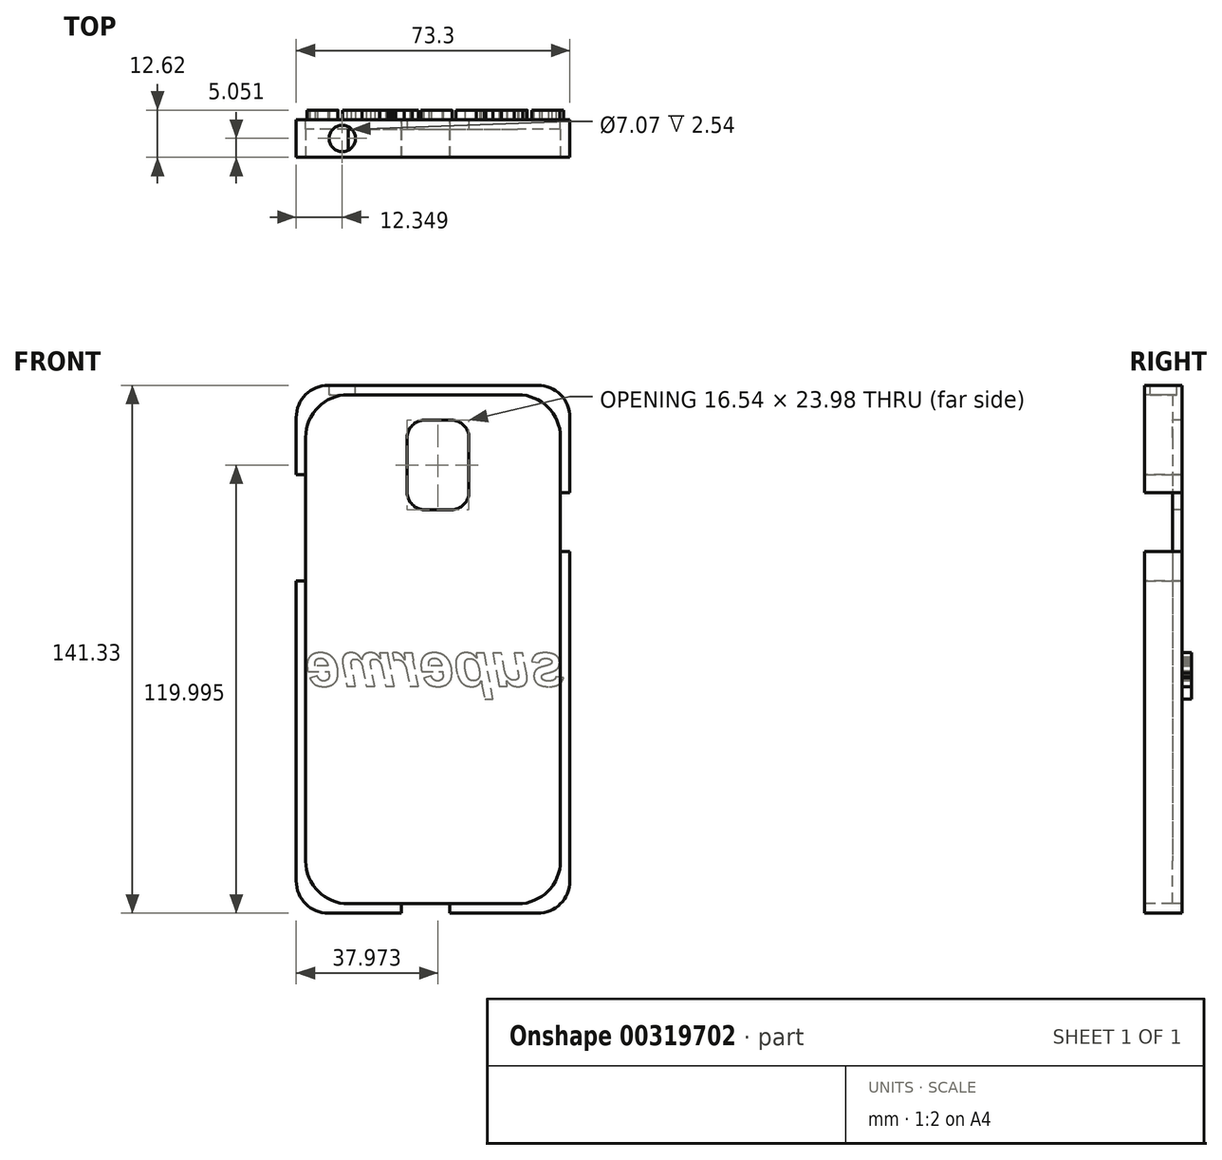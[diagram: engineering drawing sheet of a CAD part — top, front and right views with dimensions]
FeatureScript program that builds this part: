
annotation { "Feature Type Name" : "Feature", "Feature Type Description" : "" }
export const myFeature = defineFeature(function(context is Context, id is Id, definition is map)
    precondition{}
    {
        {
            var Q0;
            Q0=qCreatedBy(makeId("Front.planeOp"),FACE);
            var sketch = newSketch(context, id + "F0", { "sketchPlane" : qUnion([Q0])});
            skLineSegment(sketch, "E0.bottom", {"start": v(-58.25, 68.55) * mm, "end": v(15.05, 68.55) * mm});
            skLineSegment(sketch, "E0.top", {"start": v(-58.25, -72.78) * mm, "end": v(15.05, -72.78) * mm});
            skLineSegment(sketch, "E0.left", {"start": v(-58.25, 68.55) * mm, "end": v(-58.25, -72.78) * mm});
            skLineSegment(sketch, "E0.right", {"start": v(15.05, 68.55) * mm, "end": v(15.05, -72.78) * mm});
            skLineSegment(sketch, "E1.bottom", {"start": v(-23.48, 54.28) * mm, "end": v(-18.56, 54.28) * mm});
            skLineSegment(sketch, "E1.top", {"start": v(-23.48, 32.28) * mm, "end": v(-18.56, 32.28) * mm});
            skLineSegment(sketch, "E1.left", {"start": v(-26.02, 51.74) * mm, "end": v(-26.02, 34.82) * mm});
            skLineSegment(sketch, "E1.right", {"start": v(-16.02, 51.74) * mm, "end": v(-16.02, 34.82) * mm});
            skPoint(sketch, "E2.visualSharp", {"position": v(-26.02, 54.28) * mm});
            skArc(sketch, "E2.filletArc", {"start": v(-23.48, 54.28) * mm, "mid": v(-25.28, 53.54) * mm, "end": v(-26.02, 51.74) * mm});
            skPoint(sketch, "E3.visualSharp", {"position": v(-26.02, 32.28) * mm});
            skArc(sketch, "E3.filletArc", {"start": v(-26.02, 34.82) * mm, "mid": v(-25.28, 33.03) * mm, "end": v(-23.48, 32.28) * mm});
            skLineSegment(sketch, "E4.bottom", {"start": v(-52.76, -64.42) * mm, "end": v(-45.27, -64.42) * mm});
            skLineSegment(sketch, "E4.top", {"start": v(-52.76, -69.42) * mm, "end": v(-45.27, -69.42) * mm});
            skLineSegment(sketch, "E4.left", {"start": v(-53.01, -64.68) * mm, "end": v(-53.01, -69.17) * mm});
            skLineSegment(sketch, "E4.right", {"start": v(-45.01, -64.68) * mm, "end": v(-45.01, -69.17) * mm});
            skPoint(sketch, "E5.visualSharp", {"position": v(-16.02, 54.28) * mm});
            skArc(sketch, "E5.filletArc", {"start": v(-16.02, 51.74) * mm, "mid": v(-16.76, 53.54) * mm, "end": v(-18.56, 54.28) * mm});
            skPoint(sketch, "E6.visualSharp", {"position": v(-16.02, 32.28) * mm});
            skArc(sketch, "E6.filletArc", {"start": v(-18.56, 32.28) * mm, "mid": v(-16.76, 33.03) * mm, "end": v(-16.02, 34.82) * mm});
            skPoint(sketch, "E7.visualSharp", {"position": v(-53.01, -64.42) * mm});
            skArc(sketch, "E7.filletArc", {"start": v(-52.76, -64.42) * mm, "mid": v(-52.94, -64.5) * mm, "end": v(-53.01, -64.68) * mm});
            skPoint(sketch, "E8.visualSharp", {"position": v(-53.01, -69.42) * mm});
            skArc(sketch, "E8.filletArc", {"start": v(-53.01, -69.17) * mm, "mid": v(-52.94, -69.35) * mm, "end": v(-52.76, -69.42) * mm});
            skPoint(sketch, "E9.visualSharp", {"position": v(-45.01, -64.42) * mm});
            skArc(sketch, "E9.filletArc", {"start": v(-45.01, -64.68) * mm, "mid": v(-45.09, -64.5) * mm, "end": v(-45.27, -64.42) * mm});
            skPoint(sketch, "E10.visualSharp", {"position": v(-45.01, -69.42) * mm});
            skArc(sketch, "E10.filletArc", {"start": v(-45.27, -69.42) * mm, "mid": v(-45.09, -69.35) * mm, "end": v(-45.01, -69.17) * mm});
            skLineSegment(sketch, "E11.0", {"start": v(-55.71, 66) * mm, "end": v(12.51, 66) * mm});
            skLineSegment(sketch, "E11.1", {"start": v(-55.71, 66) * mm, "end": v(-55.71, -70.24) * mm});
            skLineSegment(sketch, "E11.2", {"start": v(-55.71, -70.24) * mm, "end": v(12.51, -70.24) * mm});
            skLineSegment(sketch, "E11.3", {"start": v(12.51, 66) * mm, "end": v(12.51, -70.24) * mm});
            skSolve(sketch);
        }
        {
            var Q0;
            Q0=makeQuery(id+"F0.imprint","IMPRINT",FACE,{"disambiguationData":[TD([[makeQuery(id+"F0.imprint","IMPRINT",EDGE,{"derivedFrom":sQuery(id+"F0.wireOp",EDGE,"E0.bottom")}),-1.0]])]});
            extrude(context, id + "F1", {"entities" : qUnion([Q0]), "oppositeDirection" : true, "depth" : 10.08 * mm});
        }
        {
            var Q0;
            Q0=makeQuery(id+"F1.opExtrude","CAP_FACE",FACE,{"disambiguationData":[OSD([sQuery(id+"F0.wireOp",EDGE,"E0.bottom"),sQuery(id+"F0.wireOp",EDGE,"E0.top"),sQuery(id+"F0.wireOp",EDGE,"E0.left"),sQuery(id+"F0.wireOp",EDGE,"E0.right"),sQuery(id+"F0.wireOp",EDGE,"E11.0"),sQuery(id+"F0.wireOp",EDGE,"E11.1"),sQuery(id+"F0.wireOp",EDGE,"E11.2"),sQuery(id+"F0.wireOp",EDGE,"E11.3")])],"isStart":false});
            var sketch = newSketch(context, id + "F2", { "sketchPlane" : qUnion([Q0])});
            skSolve(sketch);
        }
        {
            var Q0;
            Q0=makeQuery(id+"F2.imprint","IMPRINT",FACE,{"disambiguationData":[TD([[makeQuery(id+"F2.imprint","IMPRINT",EDGE,{"derivedFrom":makeQuery(id+"F1.opExtrude","CAP_EDGE",EDGE,{"disambiguationData":[OSD([sQuery(id+"F0.wireOp",EDGE,"E11.0")])],"isStart":false})}),1.0]])]});
            var Q1;
            Q1=makeQuery(id+"F2.imprint","IMPRINT",FACE,{"disambiguationData":[TD([[makeQuery(id+"F2.imprint","IMPRINT",EDGE,{"derivedFrom":makeQuery(id+"F1.opExtrude","CAP_EDGE",EDGE,{"disambiguationData":[OSD([sQuery(id+"F0.wireOp",EDGE,"E0.bottom")])],"isStart":false})}),1.0]])]});
            extrude(context, id + "F3", {"entities" : qUnion([Q0, Q1]), "operationType" : NewBodyOperationType.ADD, "oppositeDirection" : true, "depth" : 2.54 * mm});
        }
        {
            var Q0;
            {var subQ0=sQuery(id+"F0.wireOp",EDGE,"E0.right");var subQ1=sQuery(id+"F0.wireOp",EDGE,"E0.left");var subQ2=sQuery(id+"F0.wireOp",EDGE,"E0.top");var subQ3=sQuery(id+"F0.wireOp",EDGE,"E0.bottom");Q0=makeQuery(id+"F3.boolean.opBoolean","MERGE",FACE,{"derivedFrom":[makeQuery(id+"F1.opExtrude","CAP_FACE",FACE,{"disambiguationData":[OSD([subQ3,subQ2,subQ1,subQ0,sQuery(id+"F0.wireOp",EDGE,"E11.0"),sQuery(id+"F0.wireOp",EDGE,"E11.1"),sQuery(id+"F0.wireOp",EDGE,"E11.2"),sQuery(id+"F0.wireOp",EDGE,"E11.3")])],"isStart":false}),makeQuery(id+"F3.opExtrude","CAP_FACE",FACE,{"disambiguationData":[OSD([subQ3,subQ2,subQ1,subQ0])],"isStart":true})]});}
            var sketch = newSketch(context, id + "F4", { "sketchPlane" : qUnion([Q0])});
            skSolve(sketch);
        }
        {
            var Q0;
            Q0=makeQuery(id+"F1.opExtrude","SWEPT_FACE",FACE,{"disambiguationData":[OSD([sQuery(id+"F0.wireOp",EDGE,"E0.left")])]});
            var sketch = newSketch(context, id + "F5", { "sketchPlane" : qUnion([Q0])});
            skLineSegment(sketch, "E12.bottom", {"start": v(-10.08, 44.57) * mm, "end": v(0, 44.57) * mm});
            skLineSegment(sketch, "E12.top", {"start": v(-10.08, 16.2) * mm, "end": v(0, 16.2) * mm});
            skLineSegment(sketch, "E12.left", {"start": v(0, 44.57) * mm, "end": v(0, 16.2) * mm});
            skLineSegment(sketch, "E12.right", {"start": v(-10.08, 44.57) * mm, "end": v(-10.08, 16.2) * mm});
            skSolve(sketch);
        }
        {
            var Q0;
            Q0=makeQuery(id+"F1.opExtrude","SWEPT_FACE",FACE,{"disambiguationData":[OSD([sQuery(id+"F0.wireOp",EDGE,"E0.right")])]});
            var sketch = newSketch(context, id + "F6", { "sketchPlane" : qUnion([Q0])});
            skLineSegment(sketch, "E13.bottom", {"start": v(0, 39.75) * mm, "end": v(10.08, 39.75) * mm});
            skLineSegment(sketch, "E13.top", {"start": v(0, 24.1) * mm, "end": v(10.08, 24.1) * mm});
            skLineSegment(sketch, "E13.left", {"start": v(10.08, 39.75) * mm, "end": v(10.08, 24.1) * mm});
            skLineSegment(sketch, "E13.right", {"start": v(0, 39.75) * mm, "end": v(0, 24.1) * mm});
            skSolve(sketch);
        }
        {
            var Q0;
            Q0=makeQuery(id+"F1.opExtrude","SWEPT_FACE",FACE,{"disambiguationData":[OSD([sQuery(id+"F0.wireOp",EDGE,"E0.top")])]});
            var sketch = newSketch(context, id + "F7", { "sketchPlane" : qUnion([Q0])});
            skLineSegment(sketch, "E14.bottom", {"start": v(-30.14, -10.08) * mm, "end": v(-17.14, -10.08) * mm});
            skLineSegment(sketch, "E14.top", {"start": v(-30.14, 0) * mm, "end": v(-17.14, 0) * mm});
            skLineSegment(sketch, "E14.left", {"start": v(-30.14, 0) * mm, "end": v(-30.14, -10.08) * mm});
            skLineSegment(sketch, "E14.right", {"start": v(-17.14, 0) * mm, "end": v(-17.14, -10.08) * mm});
            skSolve(sketch);
        }
        {
            var Q0;
            Q0=makeQuery(id+"F7.imprint","IMPRINT",FACE,{"disambiguationData":[TD([[makeQuery(id+"F7.imprint","IMPRINT",EDGE,{"derivedFrom":sQuery(id+"F7.wireOp",EDGE,"E14.bottom")}),1.0]])]});
            var Q1;
            Q1=makeQuery(id+"F1.opExtrude","SWEPT_FACE",FACE,{"disambiguationData":[OSD([sQuery(id+"F0.wireOp",EDGE,"E11.2")])]});
            extrude(context, id + "F8", {"entities" : qUnion([Q0]), "operationType" : NewBodyOperationType.REMOVE, "endBound" : BoundingType.UP_TO_SURFACE, "oppositeDirection" : true, "endBoundEntityFace" : qUnion([Q1]), "depth" : 25.4 * mm});
        }
        {
            var Q0;
            Q0=makeQuery(id+"F5.imprint","IMPRINT",FACE,{"disambiguationData":[TD([[makeQuery(id+"F5.imprint","IMPRINT",EDGE,{"derivedFrom":sQuery(id+"F5.wireOp",EDGE,"E12.bottom")}),-1.0]])]});
            var Q1;
            Q1=makeQuery(id+"F1.opExtrude","SWEPT_FACE",FACE,{"disambiguationData":[OSD([sQuery(id+"F0.wireOp",EDGE,"E11.1")])]});
            extrude(context, id + "F9", {"entities" : qUnion([Q0]), "operationType" : NewBodyOperationType.REMOVE, "endBound" : BoundingType.UP_TO_SURFACE, "oppositeDirection" : true, "endBoundEntityFace" : qUnion([Q1]), "depth" : 25.4 * mm});
        }
        {
            var Q0;
            Q0=makeQuery(id+"F6.imprint","IMPRINT",FACE,{"disambiguationData":[TD([[makeQuery(id+"F6.imprint","IMPRINT",EDGE,{"derivedFrom":sQuery(id+"F6.wireOp",EDGE,"E13.bottom")}),-1.0]])]});
            var Q1;
            Q1=makeQuery(id+"F1.opExtrude","SWEPT_FACE",FACE,{"disambiguationData":[OSD([sQuery(id+"F0.wireOp",EDGE,"E11.3")])]});
            extrude(context, id + "F10", {"entities" : qUnion([Q0]), "operationType" : NewBodyOperationType.REMOVE, "endBound" : BoundingType.UP_TO_SURFACE, "oppositeDirection" : true, "endBoundEntityFace" : qUnion([Q1]), "depth" : 25.4 * mm});
        }
        {
            var Q0;
            Q0=makeQuery(id+"F1.opExtrude","SWEPT_FACE",FACE,{"disambiguationData":[OSD([sQuery(id+"F0.wireOp",EDGE,"E0.bottom")])]});
            var sketch = newSketch(context, id + "F11", { "sketchPlane" : qUnion([Q0])});
            skCircle(sketch, "E15", {"center": v(-45.9, 5.05) * mm, "radius": 3.53 * mm});
            skSolve(sketch);
        }
        {
            var Q0;
            Q0=makeQuery(id+"F11.imprint","IMPRINT",FACE,{"disambiguationData":[TD([[makeQuery(id+"F11.imprint","IMPRINT",EDGE,{"derivedFrom":sQuery(id+"F11.wireOp",EDGE,"E15")}),1.0]])]});
            var Q1;
            Q1=makeQuery(id+"F1.opExtrude","SWEPT_FACE",FACE,{"disambiguationData":[OSD([sQuery(id+"F0.wireOp",EDGE,"E11.0")])]});
            extrude(context, id + "F12", {"entities" : qUnion([Q0]), "operationType" : NewBodyOperationType.REMOVE, "endBound" : BoundingType.UP_TO_SURFACE, "oppositeDirection" : true, "endBoundEntityFace" : qUnion([Q1]), "depth" : 25.4 * mm});
        }
        {
            var Q0;
            Q0=makeQuery(id+"F1.opExtrude","SWEPT_EDGE",EDGE,{"disambiguationData":[OSD([sQuery(id+"F0.wireOp",EDGE,"E0.bottom"),sQuery(id+"F0.wireOp",EDGE,"E0.right")])]});
            var Q1;
            Q1=makeQuery(id+"F1.opExtrude","SWEPT_EDGE",EDGE,{"disambiguationData":[OSD([sQuery(id+"F0.wireOp",EDGE,"E0.bottom"),sQuery(id+"F0.wireOp",EDGE,"E0.left")])]});
            var Q2;
            Q2=makeQuery(id+"F1.opExtrude","SWEPT_EDGE",EDGE,{"disambiguationData":[OSD([sQuery(id+"F0.wireOp",EDGE,"E0.top"),sQuery(id+"F0.wireOp",EDGE,"E0.right")])]});
            var Q3;
            Q3=makeQuery(id+"F1.opExtrude","SWEPT_EDGE",EDGE,{"disambiguationData":[OSD([sQuery(id+"F0.wireOp",EDGE,"E0.top"),sQuery(id+"F0.wireOp",EDGE,"E0.left")])]});
            fillet(context, id + "F13", {"entities" : qUnion([Q0, Q1, Q2, Q3]), "radius" : 8.64 * mm, "tangentPropagation" : true, "allowEdgeOverflow" : false});
        }
        {
            var Q0;
            Q0=makeQuery(id+"F1.opExtrude","SWEPT_EDGE",EDGE,{"disambiguationData":[OSD([sQuery(id+"F0.wireOp",EDGE,"E11.0"),sQuery(id+"F0.wireOp",EDGE,"E11.1")])]});
            var Q1;
            Q1=makeQuery(id+"F1.opExtrude","SWEPT_EDGE",EDGE,{"disambiguationData":[OSD([sQuery(id+"F0.wireOp",EDGE,"E11.2"),sQuery(id+"F0.wireOp",EDGE,"E11.3")])]});
            var Q2;
            Q2=makeQuery(id+"F1.opExtrude","SWEPT_EDGE",EDGE,{"disambiguationData":[OSD([sQuery(id+"F0.wireOp",EDGE,"E11.0"),sQuery(id+"F0.wireOp",EDGE,"E11.3")])]});
            var Q3;
            Q3=makeQuery(id+"F1.opExtrude","SWEPT_EDGE",EDGE,{"disambiguationData":[OSD([sQuery(id+"F0.wireOp",EDGE,"E11.1"),sQuery(id+"F0.wireOp",EDGE,"E11.2")])]});
            fillet(context, id + "F14", {"entities" : qUnion([Q0, Q1, Q2, Q3]), "radius" : 11.43 * mm, "tangentPropagation" : true, "allowEdgeOverflow" : false});
        }
        {
            var Q0;
            Q0=makeQuery(id+"F3.opExtrude","CAP_FACE",FACE,{"disambiguationData":[OSD([sQuery(id+"F0.wireOp",EDGE,"E0.bottom"),sQuery(id+"F0.wireOp",EDGE,"E0.top"),sQuery(id+"F0.wireOp",EDGE,"E0.left"),sQuery(id+"F0.wireOp",EDGE,"E0.right")])],"isStart":false});
            var sketch = newSketch(context, id + "F15", { "sketchPlane" : qUnion([Q0])});
            skLineSegment(sketch, "E16.bottom", {"start": v(-28.55, 59.2) * mm, "end": v(-12, 59.2) * mm});
            skLineSegment(sketch, "E16.top", {"start": v(-28.55, 35.23) * mm, "end": v(-12, 35.23) * mm});
            skLineSegment(sketch, "E16.left", {"start": v(-28.55, 59.2) * mm, "end": v(-28.55, 35.23) * mm});
            skLineSegment(sketch, "E16.right", {"start": v(-12, 59.2) * mm, "end": v(-12, 35.23) * mm});
            skSolve(sketch);
        }
        {
            var Q0;
            Q0=makeQuery(id+"F15.imprint","IMPRINT",FACE,{"disambiguationData":[TD([[makeQuery(id+"F15.imprint","IMPRINT",EDGE,{"derivedFrom":sQuery(id+"F15.wireOp",EDGE,"E16.bottom")}),-1.0]])]});
            var Q1;
            {var subQ0=sQuery(id+"F0.wireOp",EDGE,"E0.right");var subQ1=sQuery(id+"F0.wireOp",EDGE,"E0.left");var subQ2=sQuery(id+"F0.wireOp",EDGE,"E0.top");var subQ3=sQuery(id+"F0.wireOp",EDGE,"E0.bottom");Q1=makeQuery(id+"F3.boolean.opBoolean","MERGE",FACE,{"derivedFrom":[makeQuery(id+"F1.opExtrude","CAP_FACE",FACE,{"disambiguationData":[OSD([subQ3,subQ2,subQ1,subQ0,sQuery(id+"F0.wireOp",EDGE,"E11.0"),sQuery(id+"F0.wireOp",EDGE,"E11.1"),sQuery(id+"F0.wireOp",EDGE,"E11.2"),sQuery(id+"F0.wireOp",EDGE,"E11.3")])],"isStart":false}),makeQuery(id+"F3.opExtrude","CAP_FACE",FACE,{"disambiguationData":[OSD([subQ3,subQ2,subQ1,subQ0])],"isStart":true})]});}
            extrude(context, id + "F16", {"entities" : qUnion([Q0]), "operationType" : NewBodyOperationType.REMOVE, "endBound" : BoundingType.UP_TO_SURFACE, "oppositeDirection" : true, "endBoundEntityFace" : qUnion([Q1]), "depth" : 25.4 * mm});
        }
        {
            var Q0;
            Q0=makeQuery(id+"F4.imprint","IMPRINT",FACE,{"disambiguationData":[TD([[makeQuery(id+"F4.imprint","IMPRINT",EDGE,{"derivedFrom":makeQuery(id+"F1.opExtrude","CAP_EDGE",EDGE,{"disambiguationData":[OSD([sQuery(id+"F0.wireOp",EDGE,"E0.bottom")])],"isStart":false})}),1.0]])]});
            var sketch = newSketch(context, id + "F17", { "sketchPlane" : qUnion([Q0])});
            skText(sketch, "E17", { "text": "superme", "fontName": "Arimo-BoldItalic.ttf"});
            const initialGuessF17  = {"E17": [-0.01352, -0.01197, 1, 0, 0.01197]};
            skSetInitialGuess(sketch, initialGuessF17);
            skSolve(sketch);
        }
        {
            var Q0;
            Q0 = qSketchRegion(id + "F17", true);
            extrude(context, id + "F18", {"entities" : qUnion([Q0]), "operationType" : NewBodyOperationType.ADD, "depth" : 2.54 * mm});
        }
        {
            var Q0;
            Q0=makeQuery(id+"F16.boolean.opBoolean","COPY",EDGE,{"derivedFrom":makeQuery(id+"F16.opExtrude","SWEPT_EDGE",EDGE,{"disambiguationData":[OSD([sQuery(id+"F15.wireOp",EDGE,"E16.bottom"),sQuery(id+"F15.wireOp",EDGE,"E16.right")])]})});
            var Q1;
            Q1=makeQuery(id+"F16.boolean.opBoolean","COPY",EDGE,{"derivedFrom":makeQuery(id+"F16.opExtrude","SWEPT_EDGE",EDGE,{"disambiguationData":[OSD([sQuery(id+"F15.wireOp",EDGE,"E16.top"),sQuery(id+"F15.wireOp",EDGE,"E16.left")])]})});
            var Q2;
            Q2=makeQuery(id+"F16.boolean.opBoolean","COPY",EDGE,{"derivedFrom":makeQuery(id+"F16.opExtrude","SWEPT_EDGE",EDGE,{"disambiguationData":[OSD([sQuery(id+"F15.wireOp",EDGE,"E16.top"),sQuery(id+"F15.wireOp",EDGE,"E16.right")])]})});
            var Q3;
            Q3=makeQuery(id+"F16.boolean.opBoolean","COPY",EDGE,{"derivedFrom":makeQuery(id+"F16.opExtrude","SWEPT_EDGE",EDGE,{"disambiguationData":[OSD([sQuery(id+"F15.wireOp",EDGE,"E16.bottom"),sQuery(id+"F15.wireOp",EDGE,"E16.left")])]})});
            fillet(context, id + "F19", {"entities" : qUnion([Q0, Q1, Q2, Q3]), "radius" : 4.7 * mm, "tangentPropagation" : true, "allowEdgeOverflow" : false});
        }
    });
